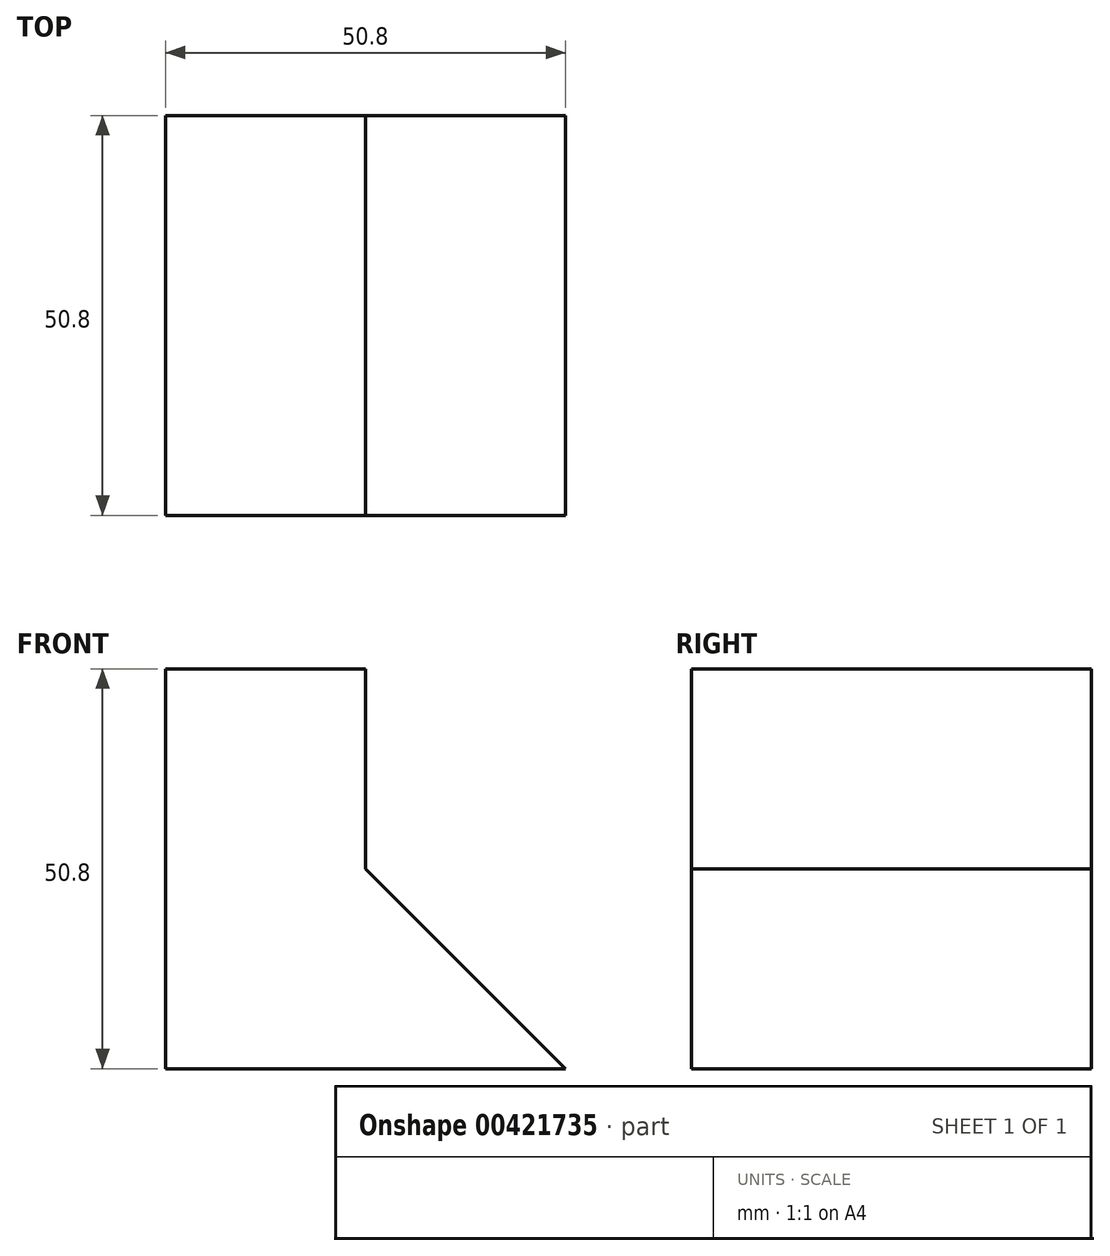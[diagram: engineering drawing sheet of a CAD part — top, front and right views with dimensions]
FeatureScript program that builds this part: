
annotation { "Feature Type Name" : "Feature", "Feature Type Description" : "" }
export const myFeature = defineFeature(function(context is Context, id is Id, definition is map)
    precondition{}
    {
        {
            var Q0;
            Q0=qCreatedBy(makeId("Front.planeOp"),FACE);
            var sketch = newSketch(context, id + "F0", { "sketchPlane" : qUnion([Q0])});
            skLineSegment(sketch, "E0", {"start": v(0, 0) * mm, "end": v(0, 50.8) * mm});
            skLineSegment(sketch, "E1", {"start": v(0, 0) * mm, "end": v(50.8, 0) * mm});
            skLineSegment(sketch, "E2", {"start": v(0, 50.8) * mm, "end": v(25.4, 50.8) * mm});
            skLineSegment(sketch, "E3", {"start": v(25.4, 50.8) * mm, "end": v(25.4, 25.4) * mm});
            skLineSegment(sketch, "E4", {"start": v(25.4, 25.4) * mm, "end": v(50.8, 0) * mm});
            skSolve(sketch);
        }
        {
            var Q0;
            Q0 = qSketchRegion(id + "F0", true);
            extrude(context, id + "F1", {"entities" : qUnion([Q0]), "depth" : 50.8 * mm});
        }
    });
